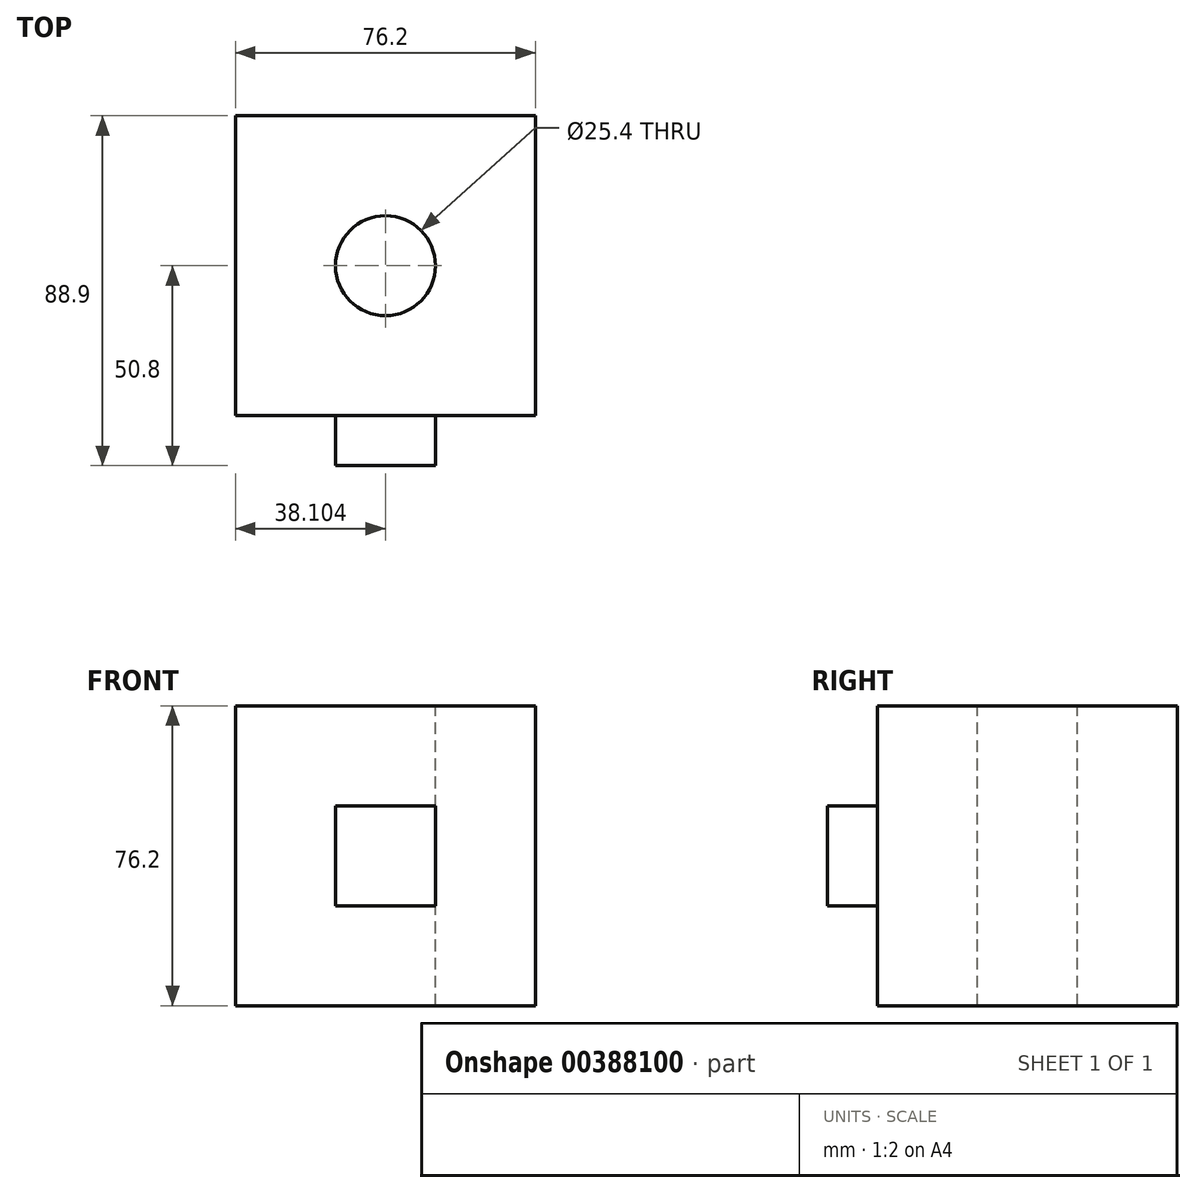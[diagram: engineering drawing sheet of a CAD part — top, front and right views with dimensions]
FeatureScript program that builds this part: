
annotation { "Feature Type Name" : "Feature", "Feature Type Description" : "" }
export const myFeature = defineFeature(function(context is Context, id is Id, definition is map)
    precondition{}
    {
        {
            var Q0;
            Q0=qCreatedBy(makeId("Front.planeOp"),FACE);
            var sketch = newSketch(context, id + "F0", { "sketchPlane" : qUnion([Q0])});
            skLineSegment(sketch, "E0.bottom", {"start": v(-39.24, 48.75) * mm, "end": v(36.96, 48.75) * mm});
            skLineSegment(sketch, "E0.top", {"start": v(-39.24, -27.45) * mm, "end": v(36.96, -27.45) * mm});
            skLineSegment(sketch, "E0.left", {"start": v(-39.24, 48.75) * mm, "end": v(-39.24, -27.45) * mm});
            skLineSegment(sketch, "E0.right", {"start": v(36.96, 48.75) * mm, "end": v(36.96, -27.45) * mm});
            skSolve(sketch);
        }
        {
            var Q0;
            Q0 = qSketchRegion(id + "F0", true);
            extrude(context, id + "F1", {"entities" : qUnion([Q0]), "depth" : 76.2 * mm});
        }
        {
            var Q0;
            Q0=makeQuery(id+"F1.opExtrude","SWEPT_FACE",FACE,{"disambiguationData":[OSD([sQuery(id+"F0.wireOp",EDGE,"E0.bottom")])]});
            var sketch = newSketch(context, id + "F2", { "sketchPlane" : qUnion([Q0])});
            skPoint(sketch, "E1", {"position": v(-1.14, -38.1) * mm});
            skSolve(sketch);
        }
        {
            var Q0;
            Q0=sQuery(id+"F2.wireOp",VERTEX,"E1");
            var Q1;
            Q1=makeQuery(id+"F1.opExtrude","SWEPT_BODY",BODY,{"disambiguationData":[OSD([sQuery(id+"F0.wireOp",EDGE,"E0.bottom"),sQuery(id+"F0.wireOp",EDGE,"E0.top"),sQuery(id+"F0.wireOp",EDGE,"E0.left"),sQuery(id+"F0.wireOp",EDGE,"E0.right")])]});
            hole(context, id + "F3", {"style" : HoleStyle.SIMPLE, "endStyle" : HoleEndStyle.THROUGH, "holeDiameter" : 25.4 * mm, "isTappedThrough" : true, "tappedDepth" : 12.7 * mm, "tapClearance" : 3, "locations" : qUnion([Q0]), "scope" : qUnion([Q1])});
        }
        {
            var Q0;
            Q0=makeQuery(id+"F1.opExtrude","CAP_FACE",FACE,{"disambiguationData":[OSD([sQuery(id+"F0.wireOp",EDGE,"E0.bottom"),sQuery(id+"F0.wireOp",EDGE,"E0.top"),sQuery(id+"F0.wireOp",EDGE,"E0.left"),sQuery(id+"F0.wireOp",EDGE,"E0.right")])],"isStart":false});
            var sketch = newSketch(context, id + "F4", { "sketchPlane" : qUnion([Q0])});
            skLineSegment(sketch, "E2.bottom", {"start": v(-13.84, 23.35) * mm, "end": v(11.56, 23.35) * mm});
            skLineSegment(sketch, "E2.top", {"start": v(-13.84, -2.05) * mm, "end": v(11.56, -2.05) * mm});
            skLineSegment(sketch, "E2.left", {"start": v(-13.84, 23.35) * mm, "end": v(-13.84, -2.05) * mm});
            skLineSegment(sketch, "E2.right", {"start": v(11.56, 23.35) * mm, "end": v(11.56, -2.05) * mm});
            skSolve(sketch);
        }
        {
            var Q0;
            Q0=makeQuery(id+"F4.imprint","IMPRINT",FACE,{"disambiguationData":[TD([[makeQuery(id+"F4.imprint","IMPRINT",EDGE,{"derivedFrom":sQuery(id+"F4.wireOp",EDGE,"E2.bottom")}),-1.0]])]});
            extrude(context, id + "F5", {"entities" : qUnion([Q0]), "operationType" : NewBodyOperationType.ADD, "depth" : 12.7 * mm});
        }
    });
